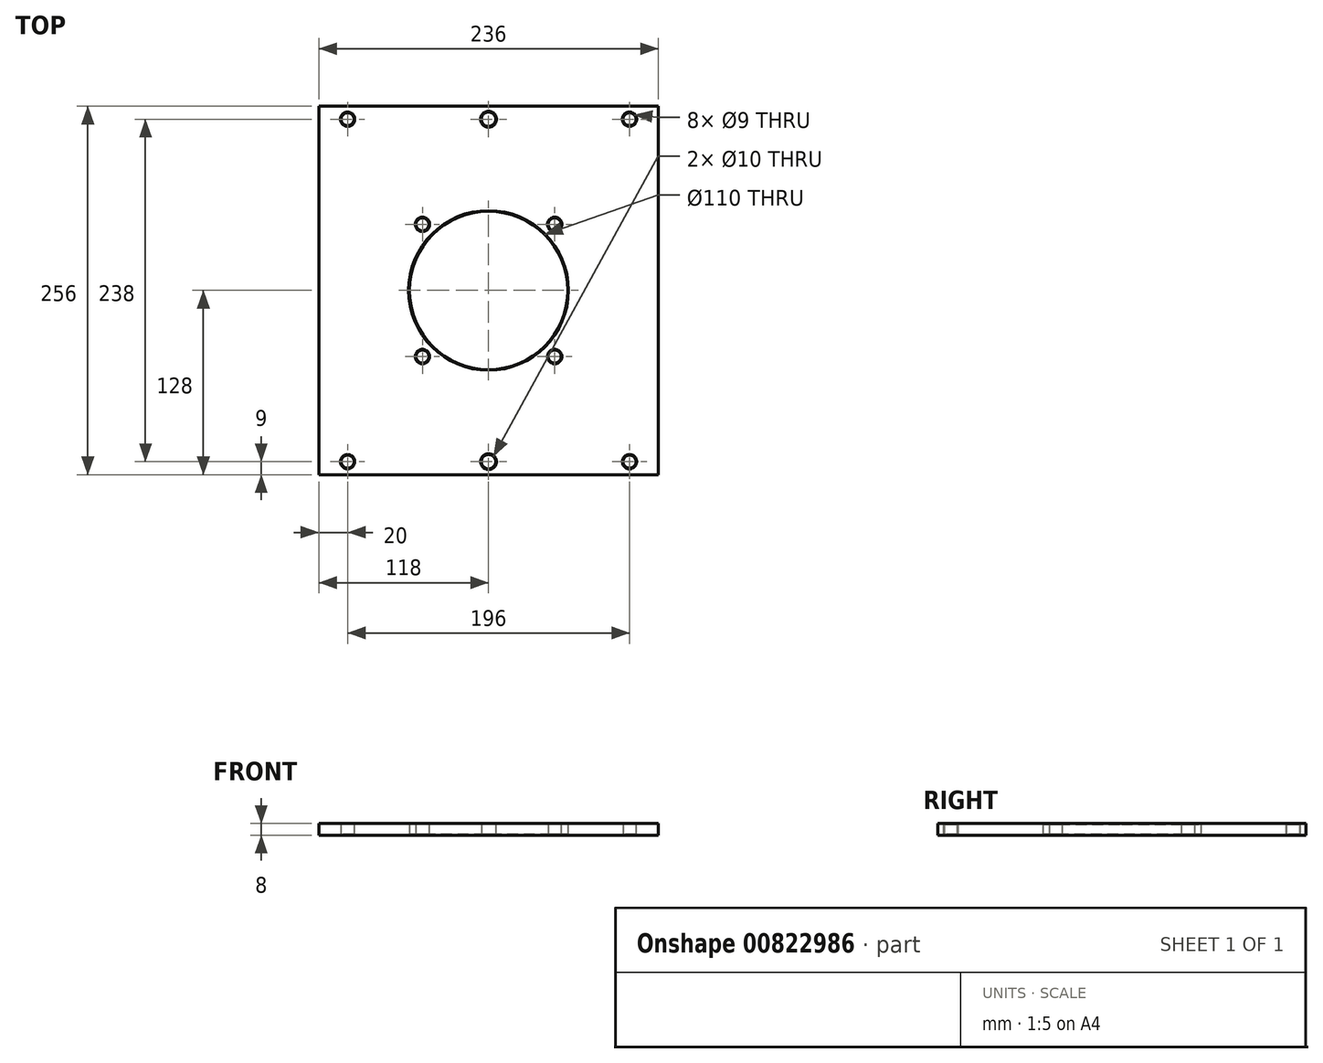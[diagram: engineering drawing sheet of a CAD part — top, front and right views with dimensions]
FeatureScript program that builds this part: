
annotation { "Feature Type Name" : "Feature", "Feature Type Description" : "" }
export const myFeature = defineFeature(function(context is Context, id is Id, definition is map)
    precondition{}
    {
        {
            var Q0;
            Q0=qCreatedBy(makeId("Top.planeOp"),FACE);
            var sketch = newSketch(context, id + "F0", { "sketchPlane" : qUnion([Q0])});
            skLineSegment(sketch, "E0.bottom", {"start": v(-118, -128) * mm, "end": v(118, -128) * mm});
            skLineSegment(sketch, "E0.top", {"start": v(-118, 128) * mm, "end": v(118, 128) * mm});
            skLineSegment(sketch, "E0.left", {"start": v(-118, -128) * mm, "end": v(-118, 128) * mm});
            skLineSegment(sketch, "E0.right", {"start": v(118, -128) * mm, "end": v(118, 128) * mm});
            skCircle(sketch, "E1", {"center": v(0, 0) * mm, "radius": 55 * mm});
            skCircle(sketch, "E2", {"center": v(0, 0) * mm, "radius": 65 * mm, "construction": true});
            skLineSegment(sketch, "E3", {"start": v(0, 0) * mm, "end": v(118, 0) * mm, "construction": true});
            skLineSegment(sketch, "E4", {"start": v(118, 0) * mm, "end": v(0, 128) * mm, "construction": true});
            skLineSegment(sketch, "E5", {"start": v(0, 128) * mm, "end": v(0, 0) * mm, "construction": true});
            skCircle(sketch, "E6", {"center": v(45.96, 45.96) * mm, "radius": 4.5 * mm});
            skLineSegment(sketch, "E7", {"start": v(0, 0) * mm, "end": v(45.96, 45.96) * mm, "construction": true});
            skCircle(sketch, "E8.MirrorC", {"center": v(-45.96, 45.96) * mm, "radius": 4.5 * mm});
            skCircle(sketch, "E9.MirrorC", {"center": v(45.96, -45.96) * mm, "radius": 4.5 * mm});
            skCircle(sketch, "E10.MirrorC", {"center": v(-45.96, -45.96) * mm, "radius": 4.5 * mm});
            skCircle(sketch, "E11", {"center": v(0, 0) * mm, "radius": 100 * mm, "construction": true});
            skLineSegment(sketch, "E12.0", {"start": v(-118, 119) * mm, "end": v(118, 119) * mm, "construction": true});
            skLineSegment(sketch, "E13.0", {"start": v(-118, -119) * mm, "end": v(118, -119) * mm, "construction": true});
            skCircle(sketch, "E14", {"center": v(98, 119) * mm, "radius": 4.5 * mm});
            skCircle(sketch, "E15.MirrorC", {"center": v(-98, 119) * mm, "radius": 4.5 * mm});
            skCircle(sketch, "E16.MirrorC", {"center": v(-98, -119) * mm, "radius": 4.5 * mm});
            skCircle(sketch, "E17.MirrorC", {"center": v(98, -119) * mm, "radius": 4.5 * mm});
            skCircle(sketch, "E18", {"center": v(0, 119) * mm, "radius": 5 * mm});
            skCircle(sketch, "E19.MirrorC", {"center": v(0, -119) * mm, "radius": 5 * mm});
            skSolve(sketch);
        }
        {
            var Q0;
            Q0 = qSketchRegion(id + "F0", true);
            extrude(context, id + "F1", {"entities" : qUnion([Q0]), "depth" : 8 * mm, "offsetDistance" : 25 * mm});
        }
        {
            var Q0;
            Q0=makeQuery(id+"F1.opExtrude","SWEPT_FACE",FACE,{"disambiguationData":[OSD([sQuery(id+"F0.wireOp",EDGE,"E16.MirrorC")])]});
            var Q1;
            Q1=makeQuery(id+"F1.opExtrude","SWEPT_FACE",FACE,{"disambiguationData":[OSD([sQuery(id+"F0.wireOp",EDGE,"E10.MirrorC")])]});
            var Q2;
            Q2=makeQuery(id+"F1.opExtrude","SWEPT_FACE",FACE,{"disambiguationData":[OSD([sQuery(id+"F0.wireOp",EDGE,"E1")])]});
            var Q3;
            Q3=makeQuery(id+"F1.opExtrude","SWEPT_FACE",FACE,{"disambiguationData":[OSD([sQuery(id+"F0.wireOp",EDGE,"E8.MirrorC")])]});
            var Q4;
            Q4=makeQuery(id+"F1.opExtrude","SWEPT_FACE",FACE,{"disambiguationData":[OSD([sQuery(id+"F0.wireOp",EDGE,"E9.MirrorC")])]});
            var Q5;
            Q5=makeQuery(id+"F1.opExtrude","SWEPT_FACE",FACE,{"disambiguationData":[OSD([sQuery(id+"F0.wireOp",EDGE,"E17.MirrorC")])]});
            var Q6;
            Q6=makeQuery(id+"F1.opExtrude","SWEPT_FACE",FACE,{"disambiguationData":[OSD([sQuery(id+"F0.wireOp",EDGE,"E15.MirrorC")])]});
            var Q7;
            Q7=makeQuery(id+"F1.opExtrude","SWEPT_FACE",FACE,{"disambiguationData":[OSD([sQuery(id+"F0.wireOp",EDGE,"E6")])]});
            var Q8;
            Q8=makeQuery(id+"F1.opExtrude","SWEPT_FACE",FACE,{"disambiguationData":[OSD([sQuery(id+"F0.wireOp",EDGE,"E14")])]});
            var Q9;
            Q9=makeQuery(id+"F1.opExtrude","SWEPT_FACE",FACE,{"disambiguationData":[OSD([sQuery(id+"F0.wireOp",EDGE,"E18")])]});
            var Q10;
            Q10=makeQuery(id+"F1.opExtrude","SWEPT_FACE",FACE,{"disambiguationData":[OSD([sQuery(id+"F0.wireOp",EDGE,"E19.MirrorC")])]});
            chamfer(context, id + "F2", {"entities" : qUnion([Q0, Q1, Q2, Q3, Q4, Q5, Q6, Q7, Q8, Q9, Q10]), "width" : 0.5 * mm, "tangentPropagation" : true});
        }
    });
